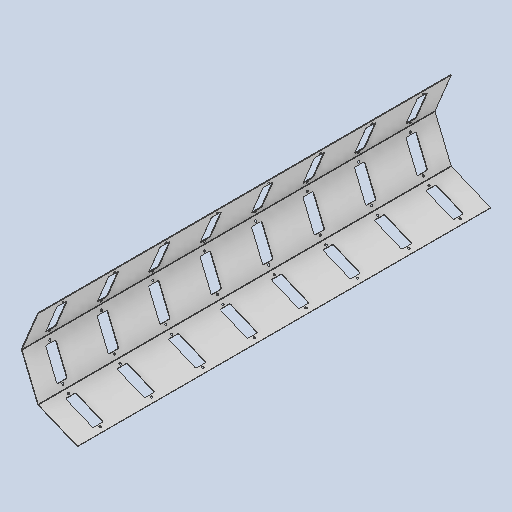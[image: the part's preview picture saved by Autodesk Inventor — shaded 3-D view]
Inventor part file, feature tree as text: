
AUTODESK INVENTOR PART (.ipt)
format: ipt  version: 2024.2 (Build 282272000, 272)  size: 388,608 bytes
history: native  units: mm
features: sheet_metal_op x3, sketch x2, extrude x1, fillet x1, pattern_circular x1, pattern_linear x1, chamfer x1, other x1, projected_geometry x1
ambient origin geometry x8: Origin, YZ Plane, XZ Plane, XY Plane, X Axis, Y Axis, Z Axis, Center Point
bodies: Body1 (feature_tree)
feature tree (12):
  sheet_metal_op  "Contour Flange3"
  extrude  "Extrusion4"  Depth=6.0mm
  fillet  "Fillet1"  Radius=1.3mm
  pattern_circular  "Circular Pattern2"  [2 undecoded]
  pattern_linear  "Rectangular Pattern2"  Spacing1=3.0mm  [1 undecoded]
  chamfer  "Corner Round1"
  sketch  "Sketch2"  dims[d58=6.0mm d59=6.0mm d70=1.3mm]
  other  "Plate6"
  sheet_metal_op  "Bend6"
  sheet_metal_op  "Corner6"
  sketch  "Sketch11"  dims[d72=1.3mm d74=506.0mm d75=3.0mm d76=3.0mm d77=1.5mm d78=6.0mm d79=3.0mm d80=2006.0mm d81=3.0mm d82=3.0mm d83=12.0mm d84=3.0mm d85=3.0mm d141=50.0mm d142=145.0mm d143=10.0mm d145=125.0mm d146=10.0mm d147=10.0mm d148=0.0mm d149=5.0mm d150=30.0mm d151=90.0deg d153=80.0mm d155=250.0mm d156=2.0mm]
  projected_geometry  "Projected Loop1"
note: 3 required parameter values undecoded (feature->parameter linkage not recoverable at this tier; creation-order binding heuristic only, values carry confidence <= 0.55)
